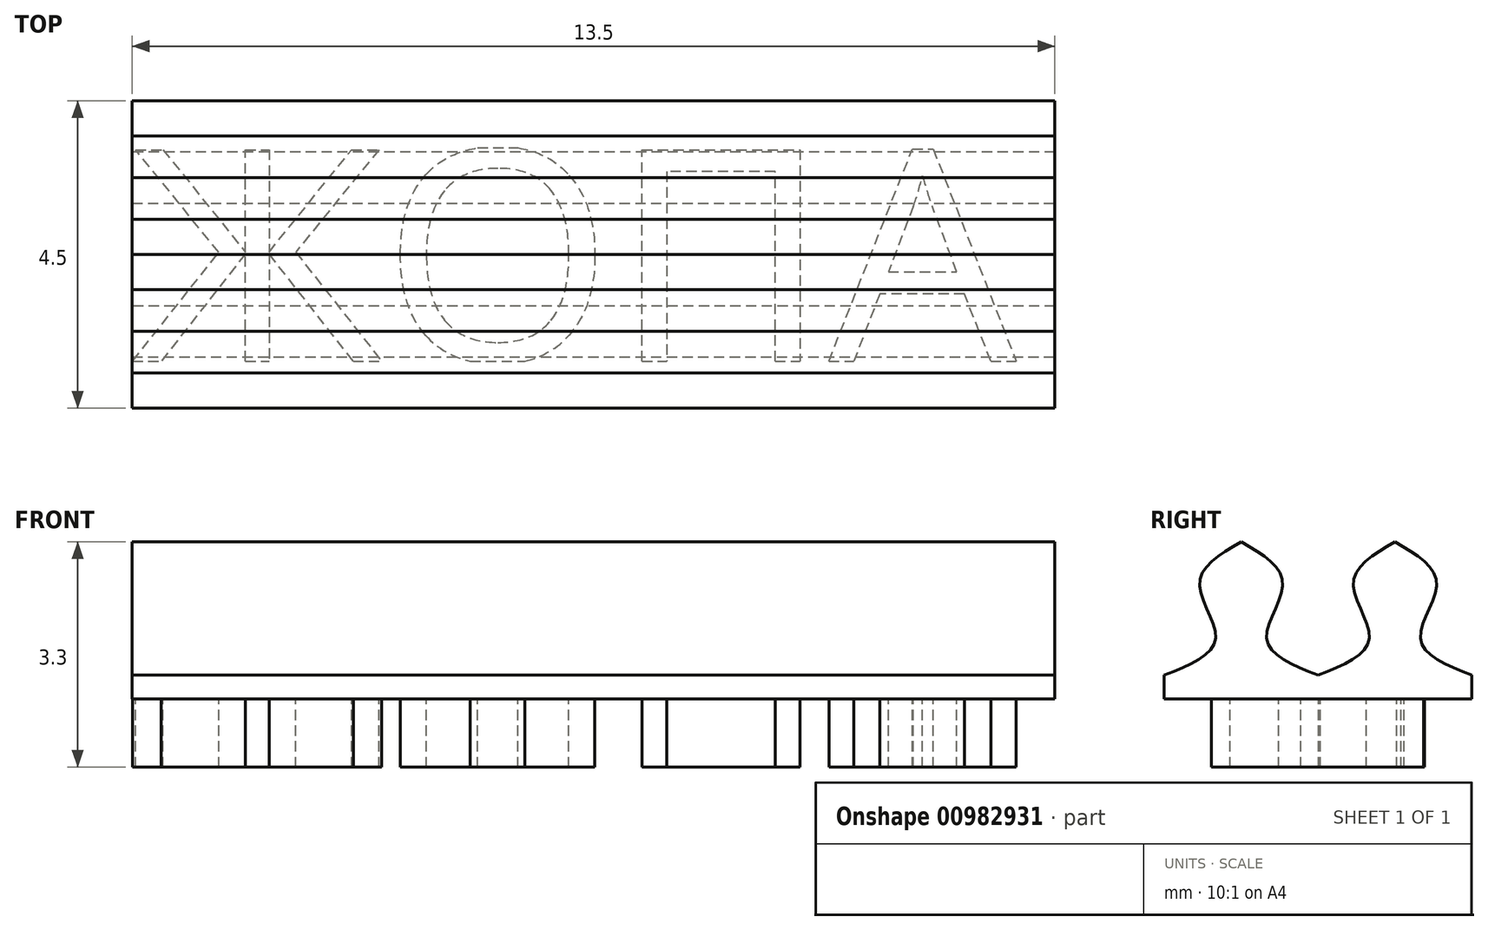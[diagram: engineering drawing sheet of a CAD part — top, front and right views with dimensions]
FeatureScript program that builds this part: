
annotation { "Feature Type Name" : "Feature", "Feature Type Description" : "" }
export const myFeature = defineFeature(function(context is Context, id is Id, definition is map)
    precondition{}
    {
        {
            var Q0;
            Q0=qCreatedBy(makeId("Top.planeOp"),FACE);
            var sketch = newSketch(context, id + "F0", { "sketchPlane" : qUnion([Q0])});
            skLineSegment(sketch, "E0.bottom", {"start": v(-6.75, 2.25) * mm, "end": v(6.75, 2.25) * mm});
            skLineSegment(sketch, "E0.top", {"start": v(-6.75, -2.25) * mm, "end": v(6.75, -2.25) * mm});
            skLineSegment(sketch, "E0.left", {"start": v(-6.75, 2.25) * mm, "end": v(-6.75, -2.25) * mm});
            skLineSegment(sketch, "E0.right", {"start": v(6.75, 2.25) * mm, "end": v(6.75, -2.25) * mm});
            skPoint(sketch, "E0.middle", {"position": v(0, 0) * mm});
            skLineSegment(sketch, "E1", {"start": v(-6.75, 1.56) * mm, "end": v(6.75, 1.56) * mm});
            skLineSegment(sketch, "E2", {"start": v(-6.75, -1.56) * mm, "end": v(6.75, -1.56) * mm});
            skText(sketch, "E3", { "text": "ЖОПА", "fontName": "OpenSans-Regular.ttf"});
            const initialGuessF0  = {"E3": [-0.00675, -0.00156, 1, 0, 0.00312]};
            skSetInitialGuess(sketch, initialGuessF0);
            skSolve(sketch);
        }
        {
            var Q0;
            {var subQ20=sQuery(id+"F0.wireOp",EDGE,"E0.top");var subQ40=sQuery(id+"F0.wireOp",EDGE,"E3.sketch_text.stroke-18");var subQ49=sQuery(id+"F0.wireOp",EDGE,"E0.bottom");Q0=qUnion([makeQuery(id+"F0.imprint","IMPRINT",FACE,{"disambiguationData":[TD([[makeQuery(id+"F0.imprint","IMPRINT",EDGE,{"derivedFrom":subQ49}),-1.0]])]}),makeQuery(id+"F0.imprint","IMPRINT",FACE,{"disambiguationData":[TD([[makeQuery(id+"F0.imprint","IMPRINT",EDGE,{"derivedFrom":sQuery(id+"F0.wireOp",EDGE,"E3.sketch_text.stroke-0")}),1.0]])]}),makeQuery(id+"F0.imprint","IMPRINT",FACE,{"disambiguationData":[TD([[makeQuery(id+"F0.imprint","IMPRINT",EDGE,{"derivedFrom":subQ40}),1.0]])]}),makeQuery(id+"F0.imprint","IMPRINT",FACE,{"disambiguationData":[TD([[makeQuery(id+"F0.imprint","IMPRINT",EDGE,{"derivedFrom":subQ20}),1.0]])]})]);}
            var Q1;
            {var subQ0=sQuery(id+"F0.wireOp",EDGE,"E3.sketch_text.stroke-35");Q1=makeQuery(id+"F0.imprint","IMPRINT",FACE,{"disambiguationData":[TD([[makeQuery(id+"F0.imprint","IMPRINT",EDGE,{"derivedFrom":subQ0}),-1.0]])]});}
            var Q2;
            {var subQ14=sQuery(id+"F0.wireOp",EDGE,"E0.top");Q2=makeQuery(id+"F0.imprint","IMPRINT",FACE,{"disambiguationData":[TD([[makeQuery(id+"F0.imprint","IMPRINT",EDGE,{"derivedFrom":subQ14}),1.0]])]});}
            var Q3;
            Q3=makeQuery(id+"F0.imprint","IMPRINT",FACE,{"disambiguationData":[TD([[makeQuery(id+"F0.imprint","IMPRINT",EDGE,{"derivedFrom":sQuery(id+"F0.wireOp",EDGE,"E3.sketch_text.stroke-26")}),1.0]])]});
            var Q4;
            {var subQ13=sQuery(id+"F0.wireOp",EDGE,"E3.sketch_text.stroke-18");Q4=makeQuery(id+"F0.imprint","IMPRINT",FACE,{"disambiguationData":[TD([[makeQuery(id+"F0.imprint","IMPRINT",EDGE,{"derivedFrom":subQ13}),-1.0]])]});}
            var Q5;
            {var subQ2=sQuery(id+"F0.wireOp",EDGE,"E3.sketch_text.stroke-42");Q5=makeQuery(id+"F0.imprint","IMPRINT",FACE,{"disambiguationData":[TD([[makeQuery(id+"F0.imprint","IMPRINT",EDGE,{"derivedFrom":subQ2}),1.0]])]});}
            var Q6;
            {var subQ0=sQuery(id+"F0.wireOp",EDGE,"E3.sketch_text.stroke-35");Q6=makeQuery(id+"F0.imprint","IMPRINT",FACE,{"disambiguationData":[TD([[makeQuery(id+"F0.imprint","IMPRINT",EDGE,{"derivedFrom":subQ0}),1.0]])]});}
            var Q7;
            {var subQ0=sQuery(id+"F0.wireOp",EDGE,"E3.sketch_text.stroke-14");Q7=makeQuery(id+"F0.imprint","IMPRINT",FACE,{"disambiguationData":[TD([[makeQuery(id+"F0.imprint","IMPRINT",EDGE,{"derivedFrom":subQ0}),1.0]])]});}
            var Q8;
            {var subQ0=sQuery(id+"F0.wireOp",EDGE,"E3.sketch_text.stroke-11");Q8=makeQuery(id+"F0.imprint","IMPRINT",FACE,{"disambiguationData":[TD([[makeQuery(id+"F0.imprint","IMPRINT",EDGE,{"derivedFrom":subQ0}),1.0]])]});}
            var Q9;
            {var subQ1=sQuery(id+"F0.wireOp",EDGE,"E0.bottom");Q9=makeQuery(id+"F0.imprint","IMPRINT",FACE,{"disambiguationData":[TD([[makeQuery(id+"F0.imprint","IMPRINT",EDGE,{"derivedFrom":subQ1}),-1.0]])]});}
            var Q10;
            {var subQ5=sQuery(id+"F0.wireOp",EDGE,"E3.sketch_text.stroke-18");Q10=makeQuery(id+"F0.imprint","IMPRINT",FACE,{"disambiguationData":[TD([[makeQuery(id+"F0.imprint","IMPRINT",EDGE,{"derivedFrom":subQ5}),1.0]])]});}
            var Q11;
            Q11=makeQuery(id+"F0.imprint","IMPRINT",FACE,{"disambiguationData":[TD([[makeQuery(id+"F0.imprint","IMPRINT",EDGE,{"derivedFrom":sQuery(id+"F0.wireOp",EDGE,"E3.sketch_text.stroke-50")}),1.0]])]});
            var Q12;
            Q12=makeQuery(id+"F0.imprint","IMPRINT",FACE,{"disambiguationData":[TD([[makeQuery(id+"F0.imprint","IMPRINT",EDGE,{"derivedFrom":sQuery(id+"F0.wireOp",EDGE,"E3.sketch_text.stroke-0")}),-1.0]])]});
            var Q13;
            Q13=makeQuery(id+"F0.imprint","IMPRINT",FACE,{"disambiguationData":[TD([[makeQuery(id+"F0.imprint","IMPRINT",EDGE,{"derivedFrom":sQuery(id+"F0.wireOp",EDGE,"E3.sketch_text.stroke-0")}),1.0]])]});
            var Q14;
            {var subQ3=sQuery(id+"F0.wireOp",EDGE,"E3.sketch_text.stroke-42");Q14=makeQuery(id+"F0.imprint","IMPRINT",FACE,{"disambiguationData":[TD([[makeQuery(id+"F0.imprint","IMPRINT",EDGE,{"derivedFrom":subQ3}),-1.0]])]});}
            var Q15;
            {var subQ0=sQuery(id+"F0.wireOp",EDGE,"E3.sketch_text.stroke-19");var subQ1=sQuery(id+"F0.wireOp",EDGE,"E2");var subQ2=makeQuery(id+"F0.imprint","INTERSECT",VERTEX,{"derivedFrom":[subQ1,subQ0]});Q15=makeQuery(id+"F0.imprint","IMPRINT",FACE,{"disambiguationData":[TD([[makeQuery(id+"F0.imprint","IMPRINT",EDGE,{"disambiguationData":[TD([[subQ2,1.0]])],"derivedFrom":subQ1}),-1.0]])]});}
            var Q16;
            {var subQ0=sQuery(id+"F0.wireOp",EDGE,"E3.sketch_text.stroke-24");var subQ1=sQuery(id+"F0.wireOp",EDGE,"E1");var subQ2=makeQuery(id+"F0.imprint","INTERSECT",VERTEX,{"derivedFrom":[subQ1,subQ0]});Q16=makeQuery(id+"F0.imprint","IMPRINT",FACE,{"disambiguationData":[TD([[makeQuery(id+"F0.imprint","IMPRINT",EDGE,{"disambiguationData":[TD([[subQ2,1.0]])],"derivedFrom":subQ1}),1.0]])]});}
            extrude(context, id + "F1", {"entities" : qUnion([Q0, Q1, Q2, Q3, Q4, Q5, Q6, Q7, Q8, Q9, Q10, Q11, Q12, Q13, Q14, Q15, Q16]), "depth" : 2.3 * mm, "offsetDistance" : 25 * mm});
        }
        {
            var Q0;
            Q0=makeQuery(id+"F0.imprint","IMPRINT",FACE,{"disambiguationData":[TD([[makeQuery(id+"F0.imprint","IMPRINT",EDGE,{"derivedFrom":sQuery(id+"F0.wireOp",EDGE,"E3.sketch_text.stroke-0")}),-1.0]])]});
            var Q1;
            {var subQ13=sQuery(id+"F0.wireOp",EDGE,"E3.sketch_text.stroke-18");Q1=makeQuery(id+"F0.imprint","IMPRINT",FACE,{"disambiguationData":[TD([[makeQuery(id+"F0.imprint","IMPRINT",EDGE,{"derivedFrom":subQ13}),-1.0]])]});}
            var Q2;
            {var subQ0=sQuery(id+"F0.wireOp",EDGE,"E3.sketch_text.stroke-35");Q2=makeQuery(id+"F0.imprint","IMPRINT",FACE,{"disambiguationData":[TD([[makeQuery(id+"F0.imprint","IMPRINT",EDGE,{"derivedFrom":subQ0}),-1.0]])]});}
            var Q3;
            {var subQ3=sQuery(id+"F0.wireOp",EDGE,"E3.sketch_text.stroke-42");Q3=makeQuery(id+"F0.imprint","IMPRINT",FACE,{"disambiguationData":[TD([[makeQuery(id+"F0.imprint","IMPRINT",EDGE,{"derivedFrom":subQ3}),-1.0]])]});}
            extrude(context, id + "F2", {"entities" : qUnion([Q0, Q1, Q2, Q3]), "operationType" : NewBodyOperationType.ADD, "oppositeDirection" : true, "depth" : 1 * mm, "offsetDistance" : 25 * mm});
        }
        {
            var Q0;
            Q0=makeQuery(id+"F1.opExtrude","SWEPT_FACE",FACE,{"disambiguationData":[OSD([sQuery(id+"F0.wireOp",EDGE,"E0.left")])]});
            var sketch = newSketch(context, id + "F3", { "sketchPlane" : qUnion([Q0])});
            skLineSegment(sketch, "E4", {"start": v(0, 0) * mm, "end": v(0, 2.3) * mm});
            skLineSegment(sketch, "E5", {"start": v(0, 2.3) * mm, "end": v(1.12, 2.3) * mm});
            skLineSegment(sketch, "E6", {"start": v(1.12, 2.3) * mm, "end": v(2.25, 2.3) * mm});
            skFitSpline(sketch, "E7", {"points": [v(2.25, 0.35) * mm, v(1.5, 0.88) * mm, v(1.73, 1.7) * mm, v(1.13, 2.3) * mm], "startDerivative": vector(-3.16, 1.25) * mm, "endDerivative": vector(-2.72, 1.6) * mm});
            skPoint(sketch, "E8.endSnap0", {"position": v(-0.34, 0) * mm});
            skFitSpline(sketch, "E9.MirrorCS", {"points": [v(0, 0.35) * mm, v(0.75, 0.88) * mm, v(0.52, 1.7) * mm, v(1.13, 2.3) * mm], "startDerivative": vector(3.16, 1.25) * mm, "endDerivative": vector(2.72, 1.6) * mm});
            skFitSpline(sketch, "E10.MirrorCS", {"points": [v(-2.25, 0.35) * mm, v(-1.5, 0.88) * mm, v(-1.73, 1.7) * mm, v(-1.13, 2.3) * mm], "startDerivative": vector(3.16, 1.25) * mm, "endDerivative": vector(2.72, 1.6) * mm});
            skFitSpline(sketch, "E11.MirrorCS", {"points": [v(0, 0.35) * mm, v(-0.75, 0.88) * mm, v(-0.52, 1.7) * mm, v(-1.13, 2.3) * mm], "startDerivative": vector(-3.16, 1.25) * mm, "endDerivative": vector(-2.72, 1.6) * mm});
            skSolve(sketch);
        }
        {
            var Q0;
            {var subQ0=sQuery(id+"F3.wireOp",EDGE,"30866dcd-1e81-418c-b22d-ae2dd3f16aeb0.MirrorCS");Q0=makeQuery(id+"F3.imprint","IMPRINT",FACE,{"disambiguationData":[TD([[makeQuery(id+"F3.imprint","IMPRINT",EDGE,{"derivedFrom":subQ0}),-1.0]])]});}
            var Q1;
            {var subQ3=sQuery(id+"F3.wireOp",EDGE,"30866dcd-1e81-418c-b22d-ae2dd3f16aeb1.MirrorCS");Q1=makeQuery(id+"F3.imprint","IMPRINT",FACE,{"disambiguationData":[TD([[makeQuery(id+"F3.imprint","IMPRINT",EDGE,{"derivedFrom":subQ3}),1.0]])]});}
            var Q2;
            {var subQ0=sQuery(id+"F3.wireOp",EDGE,"E5");Q2=makeQuery(id+"F3.imprint","IMPRINT",FACE,{"disambiguationData":[TD([[makeQuery(id+"F3.imprint","IMPRINT",EDGE,{"derivedFrom":subQ0}),-1.0]])]});}
            var Q3;
            {var subQ0=sQuery(id+"F3.wireOp",EDGE,"E6");Q3=makeQuery(id+"F3.imprint","IMPRINT",FACE,{"disambiguationData":[TD([[makeQuery(id+"F3.imprint","IMPRINT",EDGE,{"derivedFrom":subQ0}),-1.0]])]});}
            var Q4;
            {var subQ0=sQuery(id+"F3.wireOp",EDGE,"E10.MirrorCS");Q4=makeQuery(id+"F3.imprint","IMPRINT",FACE,{"disambiguationData":[TD([[makeQuery(id+"F3.imprint","IMPRINT",EDGE,{"derivedFrom":subQ0}),1.0]])]});}
            var Q5;
            {var subQ3=sQuery(id+"F3.wireOp",EDGE,"E11.MirrorCS");Q5=makeQuery(id+"F3.imprint","IMPRINT",FACE,{"disambiguationData":[TD([[makeQuery(id+"F3.imprint","IMPRINT",EDGE,{"derivedFrom":subQ3}),-1.0]])]});}
            extrude(context, id + "F4", {"entities" : qUnion([Q0, Q1, Q2, Q3, Q4, Q5]), "operationType" : NewBodyOperationType.REMOVE, "oppositeDirection" : true, "depth" : 13.5 * mm, "offsetDistance" : 25 * mm});
        }
    });
